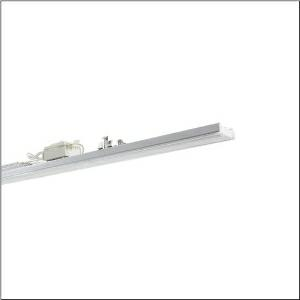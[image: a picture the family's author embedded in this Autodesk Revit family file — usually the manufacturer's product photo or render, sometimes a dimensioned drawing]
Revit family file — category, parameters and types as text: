
# Revit family: licross_11_recessed_ho_51tl11mn4exs
name_source: partatom
category: Lighting Fixtures
units: mm (PartAtom-declared; Revit-internal decimal feet)

## family parameters
Cut with Voids When Loaded = No
Host = Face
Light Source = No
Part Type = Normal
Room Calculation Point = No
Round Connector Dimension = Use Diameter
Shared = No

## types (1)
- --- (1 x LED, 14070 lm, 74.5 W, 4000K)
    Apparent Load = 75 VA
    CIE Flux Codes = 87 95 99 100 100
    Color Rendering = 80
    Color Temperature = 4000K
    Default Elevation = 1800 mm
    Description = Licross 11 Recessed HO, luminaire insert, of sheet steel, coil coated, white, length: 1.500mm, width: 66mm, height: 67mm, LED rated luminous flux: 14.070lm, light colour: 840, SDCM (Standard Deviation of Colour Matching)MacAdam ≤ 2 SDCM (initial), control gear: ON/OFF Multilumen, with plug, 3-pole, with phase selection, mains connection: 220..240V, AC, 50/60Hz, rated input power: 75W, internal wiring halogen-free, primary light control with lens, of plastic, primary optical cover: cover, of PMMA, light emission: direct distribution, primary light characteristic: symmetric, protection rating (complete): IP40, insulation class (complete): insulation class I (protective earthing), certification: CE, ENEC, VDE, UKCA, protection symbol: D if used in an environment without relevant dust loads with corresponding accessories, impact resistance: IK06, permissible ambient temperature for indoor applications: -35..+35°C, corresponds to IFS (International Featured Standards) requirements for safety and quality in the food industry, reducing of maximum allowable ambient temperature of 5°C with ceiling mounting, The light source and the operating device comply with the requirements of the Ecodesign Regulation (EU) 2019/2020 and are replaceable in accordance with this regulation, packaging unit: 1 piece
    Height = 58 mm
    Lamp = 1 x LED
    Lamp Light Flux = 14070 lm
    Lamp Power = 74.5 W
    Lamp count = 1
    Length = 1500 mm
    Luminous efficacy = 189 lm/W
    Manufacturer = Siteco
    ModVariant = No
    Model = 51TL11MN4EXS
    Mounting Place = Ceiling
    Mounting Type = Pendant
    Number of Poles = 1
    OnlyDefault = Yes
    Power Factor = 1
    Product Name = Licross 11 Recessed HO
    Product group = luminaire insert | ceiling pendant
    ProductGroupID = 901
    Protection Class = Protection class I
    Protection Degree = IP 40
    RLX_Detail_Level = 1
    RLX_Emergency_Light_Flux = 0 lm
    RLX_Emergency_Type = 0
    RLX_Emergency_Type_DB = No
    RlxData = <blob elided: 22421 chars, md5=36756ea4>
    Socket = socket
    Standby Power = 0 W
    System Light Flux = 14070 lm
    System Power = 75 W
    Type Comments = factory setting: luminous flux: 100 % | (A | C | E) | 174 mA
    Type Image = l_1296930.jpg
    URL = http://relux.com
    VarID = @adj_089499
    Voltage = 0 V
    Weight = 0.00 kg
    Width = 66 mm

## geometry (parser evidence)
native form markers: Blend x4, Sweep x10
no freeform markers — native parametric forms only
